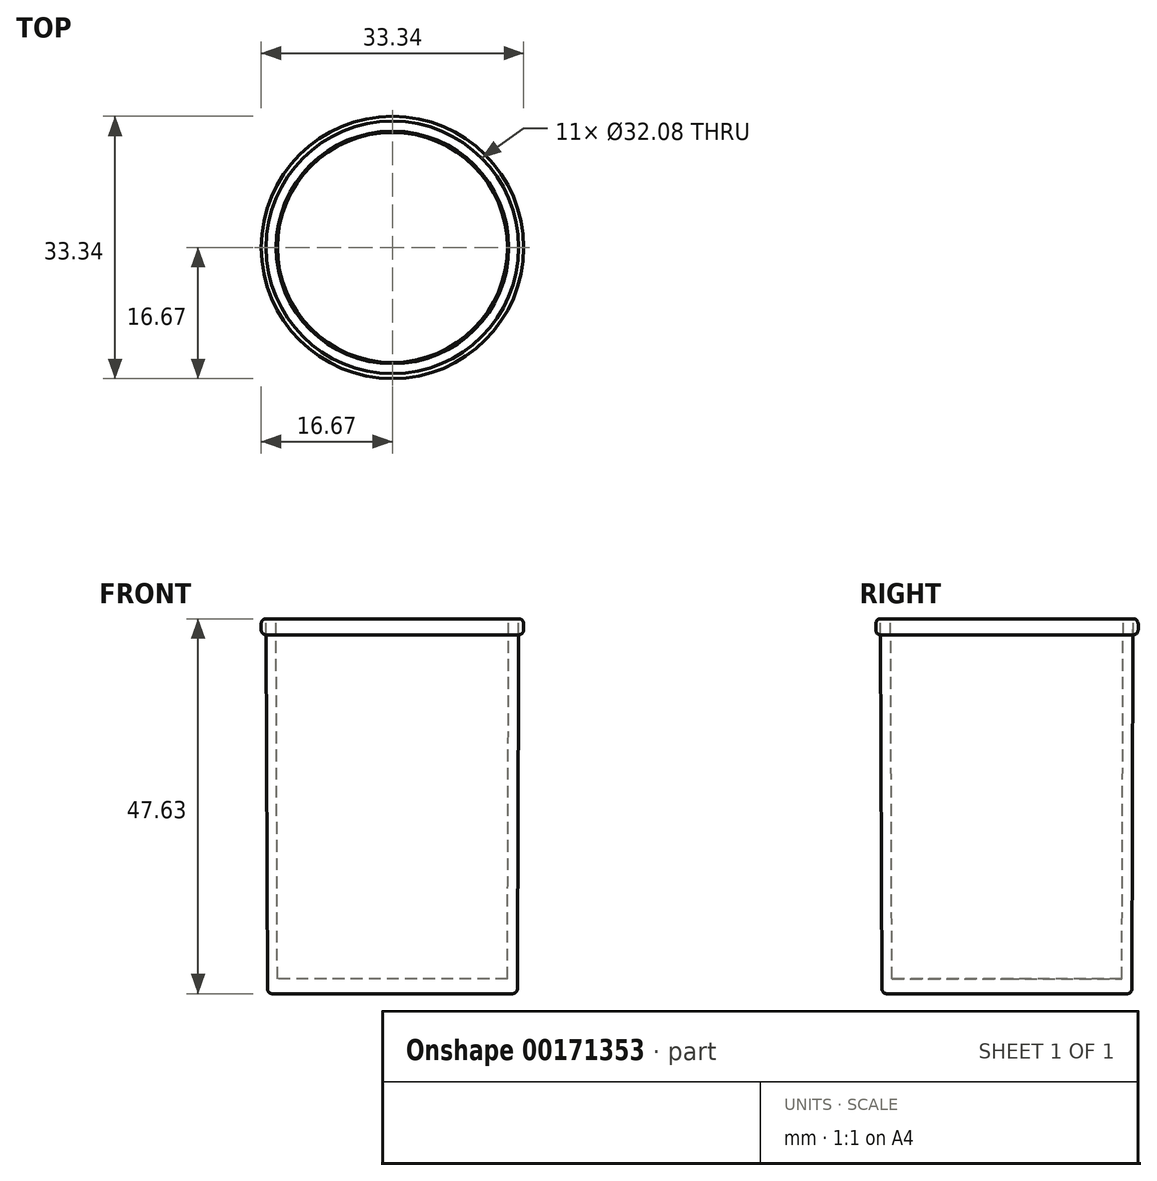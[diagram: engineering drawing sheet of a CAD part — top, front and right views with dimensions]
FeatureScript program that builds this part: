
annotation { "Feature Type Name" : "Feature", "Feature Type Description" : "" }
export const myFeature = defineFeature(function(context is Context, id is Id, definition is map)
    precondition{}
    {
        {
            var Q0;
            Q0=qCreatedBy(makeId("Top.planeOp"),FACE);
            var sketch = newSketch(context, id + "F0", { "sketchPlane" : qUnion([Q0])});
            skCircle(sketch, "E0", {"center": v(0, 0) * mm, "radius": 15.88 * mm});
            skSolve(sketch);
        }
        {
            var Q0;
            Q0 = qSketchRegion(id + "F0", true);
            extrude(context, id + "F1", {"entities" : qUnion([Q0]), "depth" : 47.62 * mm, "hasDraft" : true, "draftAngle" : .2 * degree});
        }
        {
            var Q0;
            Q0=makeQuery(id+"F1.opExtrude","CAP_FACE",FACE,{"disambiguationData":[OSD([sQuery(id+"F0.wireOp",EDGE,"E0")])],"isStart":false});
            var sketch = newSketch(context, id + "F2", { "sketchPlane" : qUnion([Q0])});
            skCircle(sketch, "E1", {"center": v(0, 0) * mm, "radius": 14.77 * mm});
            skSolve(sketch);
        }
        {
            var Q0;
            Q0=makeQuery(id+"F2.imprint","IMPRINT",FACE,{"disambiguationData":[TD([[makeQuery(id+"F2.imprint","IMPRINT",EDGE,{"derivedFrom":sQuery(id+"F2.wireOp",EDGE,"E1")}),1.0]])]});
            extrude(context, id + "F3", {"entities" : qUnion([Q0]), "operationType" : NewBodyOperationType.REMOVE, "oppositeDirection" : true, "depth" : 45.72 * mm, "hasDraft" : true, "draftAngle" : .2 * degree, "draftPullDirection" : true});
        }
        {
            var Q0;
            Q0=makeQuery(id+"F1.opExtrude","CAP_FACE",FACE,{"disambiguationData":[OSD([sQuery(id+"F0.wireOp",EDGE,"E0")])],"isStart":false});
            var sketch = newSketch(context, id + "F4", { "sketchPlane" : qUnion([Q0])});
            skCircle(sketch, "E2", {"center": v(0, 0) * mm, "radius": 16.67 * mm});
            skCircle(sketch, "E3", {"center": v(0, 0) * mm, "radius": 16.04 * mm});
            skSolve(sketch);
        }
        {
            var Q0;
            Q0 = qSketchRegion(id + "F4", true);
            extrude(context, id + "F5", {"entities" : qUnion([Q0]), "oppositeDirection" : true, "depth" : 2.03 * mm});
        }
        {
            var Q0;
            Q0=makeQuery(id+"F1.opExtrude","CAP_EDGE",EDGE,{"disambiguationData":[OSD([sQuery(id+"F0.wireOp",EDGE,"E0")])],"isStart":true});
            fillet(context, id + "F6", {"entities" : qUnion([Q0]), "radius" : 0.64 * mm, "tangentPropagation" : true, "allowEdgeOverflow" : false});
        }
        {
            var Q0;
            Q0=makeQuery(id+"F5.opExtrude","CAP_EDGE",EDGE,{"disambiguationData":[OSD([sQuery(id+"F4.wireOp",EDGE,"E2")])],"isStart":false});
            fillet(context, id + "F7", {"entities" : qUnion([Q0]), "radius" : 0.64 * mm, "tangentPropagation" : true, "allowEdgeOverflow" : false});
        }
        {
            var Q0;
            Q0=makeQuery(id+"F5.opExtrude","CAP_EDGE",EDGE,{"disambiguationData":[OSD([sQuery(id+"F4.wireOp",EDGE,"E2")])],"isStart":true});
            fillet(context, id + "F8", {"entities" : qUnion([Q0]), "radius" : 0.64 * mm, "tangentPropagation" : true, "allowEdgeOverflow" : false});
        }
    });
